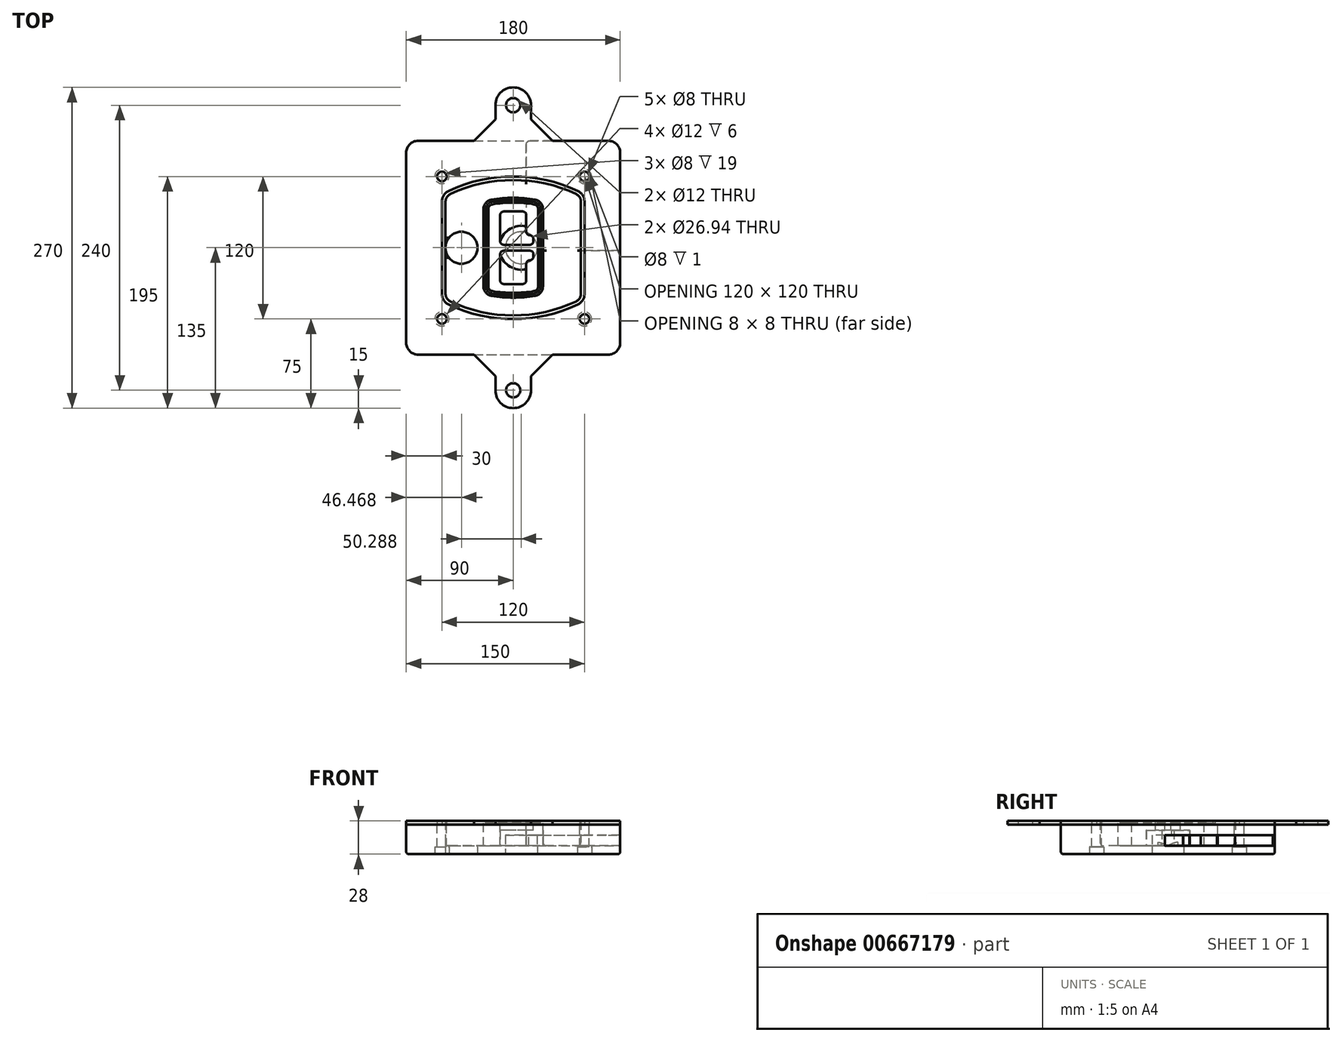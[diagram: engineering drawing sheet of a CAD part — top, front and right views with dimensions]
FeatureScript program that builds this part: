
annotation { "Feature Type Name" : "Feature", "Feature Type Description" : "" }
export const myFeature = defineFeature(function(context is Context, id is Id, definition is map)
    precondition{}
    {
        {
            var Q0;
            Q0=qCreatedBy(makeId("Top.planeOp"),FACE);
            var sketch = newSketch(context, id + "F0", { "sketchPlane" : qUnion([Q0])});
            skPoint(sketch, "E0.rect.middle", {"position": v(0, 0) * mm});
            skLineSegment(sketch, "E1.bottom", {"start": v(-80, -90) * mm, "end": v(80, -90) * mm});
            skLineSegment(sketch, "E1.top", {"start": v(-80, 90) * mm, "end": v(80, 90) * mm});
            skLineSegment(sketch, "E1.left", {"start": v(-90, -80) * mm, "end": v(-90, 80) * mm});
            skLineSegment(sketch, "E1.right", {"start": v(90, -80) * mm, "end": v(90, 80) * mm});
            skLineSegment(sketch, "E2", {"start": v(-90, 90) * mm, "end": v(90, -90) * mm, "construction": true});
            skLineSegment(sketch, "E3", {"start": v(90, 90) * mm, "end": v(-90, -90) * mm, "construction": true});
            skCircle(sketch, "E4", {"center": v(-60, 60) * mm, "radius": 4 * mm});
            skCircle(sketch, "E5", {"center": v(60, 60) * mm, "radius": 4 * mm});
            skCircle(sketch, "E6", {"center": v(60, -60) * mm, "radius": 4 * mm});
            skCircle(sketch, "E7", {"center": v(-60, -60) * mm, "radius": 4 * mm});
            skLineSegment(sketch, "E8", {"start": v(-60, 60) * mm, "end": v(60, 60) * mm, "construction": true});
            skLineSegment(sketch, "E9", {"start": v(60, 60) * mm, "end": v(60, -60) * mm, "construction": true});
            skLineSegment(sketch, "E10", {"start": v(60, -60) * mm, "end": v(-60, -60) * mm, "construction": true});
            skLineSegment(sketch, "E11", {"start": v(-60, -60) * mm, "end": v(-60, 60) * mm, "construction": true});
            skLineSegment(sketch, "E12", {"start": v(-60, 38.83) * mm, "end": v(-60, -38.83) * mm});
            skLineSegment(sketch, "E13", {"start": v(60, 38.83) * mm, "end": v(60, -38.83) * mm});
            skArc(sketch, "E14", {"start": v(54.26, 47.88) * mm, "mid": v(0, 60) * mm, "end": v(-54.26, 47.88) * mm});
            skArc(sketch, "E15", {"start": v(-54.26, -47.88) * mm, "mid": v(0, -60) * mm, "end": v(54.26, -47.88) * mm});
            skLineSegment(sketch, "E16", {"start": v(-60, 0) * mm, "end": v(60, 0) * mm, "construction": true});
            skPoint(sketch, "E17.visualSharp", {"position": v(-60, -45) * mm});
            skArc(sketch, "E17.filletArc", {"start": v(-60, -38.83) * mm, "mid": v(-58.44, -44.2) * mm, "end": v(-54.26, -47.88) * mm});
            skPoint(sketch, "E18.visualSharp", {"position": v(-60, 45) * mm});
            skArc(sketch, "E18.filletArc", {"start": v(-54.26, 47.88) * mm, "mid": v(-58.44, 44.2) * mm, "end": v(-60, 38.83) * mm});
            skPoint(sketch, "E19.visualSharp", {"position": v(60, 45) * mm});
            skArc(sketch, "E19.filletArc", {"start": v(60, 38.83) * mm, "mid": v(58.44, 44.2) * mm, "end": v(54.26, 47.88) * mm});
            skPoint(sketch, "E20.visualSharp", {"position": v(60, -45) * mm});
            skArc(sketch, "E20.filletArc", {"start": v(54.26, -47.88) * mm, "mid": v(58.44, -44.2) * mm, "end": v(60, -38.83) * mm});
            skPoint(sketch, "E21.visualSharp", {"position": v(-90, 90) * mm});
            skArc(sketch, "E21.filletArc", {"start": v(-80, 90) * mm, "mid": v(-87.07, 87.07) * mm, "end": v(-90, 80) * mm});
            skPoint(sketch, "E22.visualSharp", {"position": v(90, 90) * mm});
            skArc(sketch, "E22.filletArc", {"start": v(90, 80) * mm, "mid": v(87.07, 87.07) * mm, "end": v(80, 90) * mm});
            skPoint(sketch, "E23.visualSharp", {"position": v(90, -90) * mm});
            skArc(sketch, "E23.filletArc", {"start": v(80, -90) * mm, "mid": v(87.07, -87.07) * mm, "end": v(90, -80) * mm});
            skPoint(sketch, "E24.visualSharp", {"position": v(-90, -90) * mm});
            skArc(sketch, "E24.filletArc", {"start": v(-90, -80) * mm, "mid": v(-87.07, -87.07) * mm, "end": v(-80, -90) * mm});
            skArc(sketch, "E25.0", {"start": v(57, 38.83) * mm, "mid": v(55.9, 42.58) * mm, "end": v(52.98, 45.17) * mm});
            skLineSegment(sketch, "E25.1", {"start": v(57, 38.83) * mm, "end": v(57, -38.83) * mm});
            skArc(sketch, "E25.2", {"start": v(52.98, -45.17) * mm, "mid": v(55.9, -42.58) * mm, "end": v(57, -38.83) * mm});
            skArc(sketch, "E25.3", {"start": v(-52.98, -45.17) * mm, "mid": v(0, -57) * mm, "end": v(52.98, -45.17) * mm});
            skArc(sketch, "E25.4", {"start": v(-57, -38.83) * mm, "mid": v(-55.9, -42.58) * mm, "end": v(-52.98, -45.17) * mm});
            skArc(sketch, "E25.5", {"start": v(52.98, 45.17) * mm, "mid": v(0, 57) * mm, "end": v(-52.98, 45.17) * mm});
            skLineSegment(sketch, "E25.6", {"start": v(-57, 38.83) * mm, "end": v(-57, -38.83) * mm});
            skArc(sketch, "E25.7", {"start": v(-52.98, 45.17) * mm, "mid": v(-55.9, 42.58) * mm, "end": v(-57, 38.83) * mm});
            skArc(sketch, "E26.0", {"start": v(-55.96, 51.5) * mm, "mid": v(-61.82, 46.33) * mm, "end": v(-64, 38.83) * mm});
            skArc(sketch, "E26.1", {"start": v(55.96, 51.5) * mm, "mid": v(0, 64) * mm, "end": v(-55.96, 51.5) * mm});
            skArc(sketch, "E26.2", {"start": v(64, 38.83) * mm, "mid": v(61.82, 46.33) * mm, "end": v(55.96, 51.5) * mm});
            skLineSegment(sketch, "E26.3", {"start": v(64, 38.83) * mm, "end": v(64, -38.83) * mm});
            skArc(sketch, "E26.4", {"start": v(55.96, -51.5) * mm, "mid": v(61.82, -46.33) * mm, "end": v(64, -38.83) * mm});
            skLineSegment(sketch, "E26.5", {"start": v(-64, 38.83) * mm, "end": v(-64, -38.83) * mm});
            skArc(sketch, "E26.6", {"start": v(-55.96, -51.5) * mm, "mid": v(0, -64) * mm, "end": v(55.96, -51.5) * mm});
            skArc(sketch, "E26.7", {"start": v(-64, -38.83) * mm, "mid": v(-61.82, -46.33) * mm, "end": v(-55.96, -51.5) * mm});
            skSolve(sketch);
        }
        {
            var Q0;
            Q0=makeQuery(id+"F0.imprint","IMPRINT",FACE,{"disambiguationData":[TD([[makeQuery(id+"F0.imprint","IMPRINT",EDGE,{"derivedFrom":sQuery(id+"F0.wireOp",EDGE,"E1.bottom")}),1.0]])]});
            var Q1;
            Q1=makeQuery(id+"F0.imprint","IMPRINT",FACE,{"disambiguationData":[TD([[makeQuery(id+"F0.imprint","IMPRINT",EDGE,{"derivedFrom":sQuery(id+"F0.wireOp",EDGE,"E12")}),1.0]])]});
            var Q2;
            Q2=makeQuery(id+"F0.imprint","IMPRINT",FACE,{"disambiguationData":[TD([[makeQuery(id+"F0.imprint","IMPRINT",EDGE,{"derivedFrom":sQuery(id+"F0.wireOp",EDGE,"E25.0")}),1.0]])]});
            var Q3;
            Q3=makeQuery(id+"F0.imprint","IMPRINT",FACE,{"disambiguationData":[TD([[makeQuery(id+"F0.imprint","IMPRINT",EDGE,{"derivedFrom":sQuery(id+"F0.wireOp",EDGE,"E12")}),-1.0]])]});
            extrude(context, id + "F1", {"entities" : qUnion([Q0, Q1, Q2, Q3]), "oppositeDirection" : true, "depth" : 25 * mm, "offsetDistance" : 25 * mm});
        }
        {
            var Q0;
            Q0=makeQuery(id+"F0.imprint","IMPRINT",FACE,{"disambiguationData":[TD([[makeQuery(id+"F0.imprint","IMPRINT",EDGE,{"derivedFrom":sQuery(id+"F0.wireOp",EDGE,"E12")}),1.0]])]});
            extrude(context, id + "F2", {"entities" : qUnion([Q0]), "operationType" : NewBodyOperationType.ADD, "depth" : 3 * mm});
        }
        {
            var Q0;
            Q0=makeQuery(id+"F0.imprint","IMPRINT",FACE,{"disambiguationData":[TD([[makeQuery(id+"F0.imprint","IMPRINT",EDGE,{"derivedFrom":sQuery(id+"F0.wireOp",EDGE,"E25.0")}),1.0]])]});
            extrude(context, id + "F3", {"entities" : qUnion([Q0]), "operationType" : NewBodyOperationType.REMOVE, "oppositeDirection" : true, "depth" : 18 * mm});
        }
        {
            var Q0;
            Q0=makeQuery(id+"F2.opExtrude","CAP_FACE",FACE,{"disambiguationData":[OSD([sQuery(id+"F0.wireOp",EDGE,"E12"),sQuery(id+"F0.wireOp",EDGE,"E13"),sQuery(id+"F0.wireOp",EDGE,"E14"),sQuery(id+"F0.wireOp",EDGE,"E15"),sQuery(id+"F0.wireOp",EDGE,"E17.filletArc"),sQuery(id+"F0.wireOp",EDGE,"E18.filletArc"),sQuery(id+"F0.wireOp",EDGE,"E19.filletArc"),sQuery(id+"F0.wireOp",EDGE,"E20.filletArc"),sQuery(id+"F0.wireOp",EDGE,"E25.0"),sQuery(id+"F0.wireOp",EDGE,"E25.1"),sQuery(id+"F0.wireOp",EDGE,"E25.2"),sQuery(id+"F0.wireOp",EDGE,"E25.3"),sQuery(id+"F0.wireOp",EDGE,"E25.4"),sQuery(id+"F0.wireOp",EDGE,"E25.5"),sQuery(id+"F0.wireOp",EDGE,"E25.6"),sQuery(id+"F0.wireOp",EDGE,"E25.7")])],"isStart":false});
            var sketch = newSketch(context, id + "F4", { "sketchPlane" : qUnion([Q0])});
            skArc(sketch, "E27.0", {"start": v(-18.34, -40.45) * mm, "mid": v(0, -42) * mm, "end": v(18.34, -40.45) * mm});
            skArc(sketch, "E28.0", {"start": v(18.34, 40.45) * mm, "mid": v(0, 42) * mm, "end": v(-18.34, 40.45) * mm});
            skLineSegment(sketch, "E29", {"start": v(-25, 32.57) * mm, "end": v(-25, -32.57) * mm});
            skLineSegment(sketch, "E30", {"start": v(25, 32.57) * mm, "end": v(25, -32.57) * mm});
            skLineSegment(sketch, "E31", {"start": v(-25, 39.1) * mm, "end": v(25, 39.1) * mm, "construction": true});
            skLineSegment(sketch, "E32", {"start": v(-25, -39.1) * mm, "end": v(25, -39.1) * mm, "construction": true});
            skPoint(sketch, "E33.visualSharp", {"position": v(-25, 39.1) * mm});
            skArc(sketch, "E33.filletArc", {"start": v(-18.34, 40.45) * mm, "mid": v(-23.11, 37.73) * mm, "end": v(-25, 32.57) * mm});
            skPoint(sketch, "E34.visualSharp", {"position": v(25, 39.1) * mm});
            skArc(sketch, "E34.filletArc", {"start": v(25, 32.57) * mm, "mid": v(23.11, 37.73) * mm, "end": v(18.34, 40.45) * mm});
            skPoint(sketch, "E35.visualSharp", {"position": v(25, -39.1) * mm});
            skArc(sketch, "E35.filletArc", {"start": v(18.34, -40.45) * mm, "mid": v(23.11, -37.73) * mm, "end": v(25, -32.57) * mm});
            skPoint(sketch, "E36.visualSharp", {"position": v(-25, -39.1) * mm});
            skArc(sketch, "E36.filletArc", {"start": v(-25, -32.57) * mm, "mid": v(-23.11, -37.73) * mm, "end": v(-18.34, -40.45) * mm});
            skArc(sketch, "E37.0", {"start": v(52.98, 45.17) * mm, "mid": v(0, 57) * mm, "end": v(-52.98, 45.17) * mm});
            skArc(sketch, "E37.1", {"start": v(-52.98, 45.17) * mm, "mid": v(-55.9, 42.58) * mm, "end": v(-57, 38.83) * mm});
            skLineSegment(sketch, "E37.2", {"start": v(-57, 38.83) * mm, "end": v(-57, -38.83) * mm});
            skArc(sketch, "E37.3", {"start": v(-57, -38.83) * mm, "mid": v(-55.9, -42.58) * mm, "end": v(-52.98, -45.17) * mm});
            skArc(sketch, "E37.4", {"start": v(-52.98, -45.17) * mm, "mid": v(0, -57) * mm, "end": v(52.98, -45.17) * mm});
            skArc(sketch, "E37.5", {"start": v(52.98, -45.17) * mm, "mid": v(55.9, -42.58) * mm, "end": v(57, -38.83) * mm});
            skLineSegment(sketch, "E37.6", {"start": v(57, 38.83) * mm, "end": v(57, -38.83) * mm});
            skArc(sketch, "E37.7", {"start": v(57, 38.83) * mm, "mid": v(55.9, 42.58) * mm, "end": v(52.98, 45.17) * mm});
            skLineSegment(sketch, "E38.0", {"start": v(23, 32.57) * mm, "end": v(23, -32.57) * mm});
            skArc(sketch, "E38.1", {"start": v(18, -38.48) * mm, "mid": v(21.58, -36.44) * mm, "end": v(23, -32.57) * mm});
            skArc(sketch, "E38.2", {"start": v(-18, -38.48) * mm, "mid": v(0, -40) * mm, "end": v(18, -38.48) * mm});
            skArc(sketch, "E38.3", {"start": v(-23, -32.57) * mm, "mid": v(-21.58, -36.44) * mm, "end": v(-18, -38.48) * mm});
            skLineSegment(sketch, "E38.4", {"start": v(-23, 32.57) * mm, "end": v(-23, -32.57) * mm});
            skArc(sketch, "E38.5", {"start": v(23, 32.57) * mm, "mid": v(21.58, 36.44) * mm, "end": v(18, 38.48) * mm});
            skArc(sketch, "E38.6", {"start": v(-18, 38.48) * mm, "mid": v(-21.58, 36.44) * mm, "end": v(-23, 32.57) * mm});
            skArc(sketch, "E38.7", {"start": v(18, 38.48) * mm, "mid": v(0, 40) * mm, "end": v(-18, 38.48) * mm});
            skArc(sketch, "E39.0", {"start": v(21, 32.57) * mm, "mid": v(20.06, 35.15) * mm, "end": v(17.67, 36.5) * mm});
            skLineSegment(sketch, "E39.1", {"start": v(21, 32.57) * mm, "end": v(21, -32.57) * mm});
            skArc(sketch, "E39.2", {"start": v(17.67, -36.5) * mm, "mid": v(20.06, -35.15) * mm, "end": v(21, -32.57) * mm});
            skArc(sketch, "E39.3", {"start": v(-17.67, -36.5) * mm, "mid": v(0, -38) * mm, "end": v(17.67, -36.5) * mm});
            skArc(sketch, "E39.4", {"start": v(-21, -32.57) * mm, "mid": v(-20.06, -35.15) * mm, "end": v(-17.67, -36.5) * mm});
            skArc(sketch, "E39.5", {"start": v(17.67, 36.5) * mm, "mid": v(0, 38) * mm, "end": v(-17.67, 36.5) * mm});
            skLineSegment(sketch, "E39.6", {"start": v(-21, 32.57) * mm, "end": v(-21, -32.57) * mm});
            skArc(sketch, "E39.7", {"start": v(-17.67, 36.5) * mm, "mid": v(-20.06, 35.15) * mm, "end": v(-21, 32.57) * mm});
            skLineSegment(sketch, "E40", {"start": v(-25, 0) * mm, "end": v(25, 0) * mm, "construction": true});
            skLineSegment(sketch, "E41", {"start": v(-11, 5.5) * mm, "end": v(-11, 27.5) * mm});
            skLineSegment(sketch, "E42", {"start": v(-8, 30.5) * mm, "end": v(8, 30.5) * mm});
            skLineSegment(sketch, "E43", {"start": v(11, 27.5) * mm, "end": v(11, 13.5) * mm});
            skLineSegment(sketch, "E44", {"start": v(14, 10.5) * mm, "end": v(14, 10.5) * mm});
            skLineSegment(sketch, "E45", {"start": v(17, 7.5) * mm, "end": v(17, 5.5) * mm});
            skLineSegment(sketch, "E46", {"start": v(14, 2.5) * mm, "end": v(-8, 2.5) * mm});
            skPoint(sketch, "E47.visualSharp", {"position": v(-11, 30.5) * mm});
            skArc(sketch, "E47.filletArc", {"start": v(-8, 30.5) * mm, "mid": v(-10.12, 29.62) * mm, "end": v(-11, 27.5) * mm});
            skPoint(sketch, "E48.visualSharp", {"position": v(11, 30.5) * mm});
            skArc(sketch, "E48.filletArc", {"start": v(11, 27.5) * mm, "mid": v(10.12, 29.62) * mm, "end": v(8, 30.5) * mm});
            skPoint(sketch, "E49.visualSharp", {"position": v(11, 10.5) * mm});
            skArc(sketch, "E49.filletArc", {"start": v(11, 13.5) * mm, "mid": v(11.88, 11.38) * mm, "end": v(14, 10.5) * mm});
            skPoint(sketch, "E50.visualSharp", {"position": v(17, 10.5) * mm});
            skArc(sketch, "E50.filletArc", {"start": v(17, 7.5) * mm, "mid": v(16.12, 9.62) * mm, "end": v(14, 10.5) * mm});
            skPoint(sketch, "E51.visualSharp", {"position": v(17, 2.5) * mm});
            skArc(sketch, "E51.filletArc", {"start": v(14, 2.5) * mm, "mid": v(16.12, 3.38) * mm, "end": v(17, 5.5) * mm});
            skPoint(sketch, "E52.visualSharp", {"position": v(-11, 2.5) * mm});
            skArc(sketch, "E52.filletArc", {"start": v(-11, 5.5) * mm, "mid": v(-10.12, 3.38) * mm, "end": v(-8, 2.5) * mm});
            skLineSegment(sketch, "E53.0.MirrorCS", {"start": v(14, -2.5) * mm, "end": v(-8, -2.5) * mm});
            skArc(sketch, "E54.0.MirrorCS", {"start": v(-11, -5.5) * mm, "mid": v(-10.12, -3.38) * mm, "end": v(-8, -2.5) * mm});
            skLineSegment(sketch, "E55.0.MirrorCS", {"start": v(-11, -5.5) * mm, "end": v(-11, -27.5) * mm});
            skArc(sketch, "E56.0.MirrorCS", {"start": v(-8, -30.5) * mm, "mid": v(-10.12, -29.62) * mm, "end": v(-11, -27.5) * mm});
            skLineSegment(sketch, "E57.0.MirrorCS", {"start": v(-8, -30.5) * mm, "end": v(8, -30.5) * mm});
            skArc(sketch, "E58.0.MirrorCS", {"start": v(11, -27.5) * mm, "mid": v(10.12, -29.62) * mm, "end": v(8, -30.5) * mm});
            skLineSegment(sketch, "E59.0.MirrorCS", {"start": v(11, -27.5) * mm, "end": v(11, -13.5) * mm});
            skArc(sketch, "E60.0.MirrorCS", {"start": v(11, -13.5) * mm, "mid": v(11.88, -11.38) * mm, "end": v(14, -10.5) * mm});
            skArc(sketch, "E61.0.MirrorCS", {"start": v(17, -7.5) * mm, "mid": v(16.12, -9.62) * mm, "end": v(14, -10.5) * mm});
            skLineSegment(sketch, "E62.0.MirrorCS", {"start": v(17, -7.5) * mm, "end": v(17, -5.5) * mm});
            skArc(sketch, "E63.0.MirrorCS", {"start": v(14, -2.5) * mm, "mid": v(16.12, -3.38) * mm, "end": v(17, -5.5) * mm});
            skSolve(sketch);
        }
        {
            var Q0;
            Q0=makeQuery(id+"F4.imprint","IMPRINT",FACE,{"disambiguationData":[TD([[makeQuery(id+"F4.imprint","IMPRINT",EDGE,{"derivedFrom":sQuery(id+"F4.wireOp",EDGE,"E27.0")}),1.0]])]});
            var Q1;
            Q1=makeQuery(id+"F4.imprint","IMPRINT",FACE,{"disambiguationData":[TD([[makeQuery(id+"F4.imprint","IMPRINT",EDGE,{"derivedFrom":sQuery(id+"F4.wireOp",EDGE,"E38.0")}),-1.0]])]});
            var Q2;
            Q2=makeQuery(id+"F4.imprint","IMPRINT",FACE,{"disambiguationData":[TD([[makeQuery(id+"F4.imprint","IMPRINT",EDGE,{"derivedFrom":sQuery(id+"F4.wireOp",EDGE,"E39.0")}),1.0]])]});
            extrude(context, id + "F5", {"entities" : qUnion([Q0, Q1, Q2]), "operationType" : NewBodyOperationType.ADD, "endBound" : BoundingType.UP_TO_NEXT, "oppositeDirection" : true, "depth" : 25 * mm});
        }
        {
            var Q0;
            Q0=makeQuery(id+"F4.imprint","IMPRINT",FACE,{"disambiguationData":[TD([[makeQuery(id+"F4.imprint","IMPRINT",EDGE,{"derivedFrom":sQuery(id+"F4.wireOp",EDGE,"E38.0")}),-1.0]])]});
            extrude(context, id + "F6", {"entities" : qUnion([Q0]), "operationType" : NewBodyOperationType.REMOVE, "oppositeDirection" : true, "depth" : 2 * mm});
        }
        {
            var Q0;
            Q0=makeQuery(id+"F1.opExtrude","CAP_FACE",FACE,{"disambiguationData":[OSD([sQuery(id+"F0.wireOp",EDGE,"E1.bottom"),sQuery(id+"F0.wireOp",EDGE,"E1.top"),sQuery(id+"F0.wireOp",EDGE,"E1.left"),sQuery(id+"F0.wireOp",EDGE,"E1.right"),sQuery(id+"F0.wireOp",EDGE,"E4"),sQuery(id+"F0.wireOp",EDGE,"E5"),sQuery(id+"F0.wireOp",EDGE,"E6"),sQuery(id+"F0.wireOp",EDGE,"E7"),sQuery(id+"F0.wireOp",EDGE,"E21.filletArc"),sQuery(id+"F0.wireOp",EDGE,"E22.filletArc"),sQuery(id+"F0.wireOp",EDGE,"E23.filletArc"),sQuery(id+"F0.wireOp",EDGE,"E24.filletArc")])],"isStart":false});
            var sketch = newSketch(context, id + "F7", { "sketchPlane" : qUnion([Q0])});
            skCircle(sketch, "E64", {"center": v(6.76, 0) * mm, "radius": 13.47 * mm});
            skCircle(sketch, "E65", {"center": v(-43.53, 0) * mm, "radius": 13.47 * mm});
            skLineSegment(sketch, "E66", {"start": v(90, 0) * mm, "end": v(-90, 0) * mm});
            skCircle(sketch, "E67", {"center": v(6.76, 0) * mm, "radius": 18.47 * mm});
            skCircle(sketch, "E68", {"center": v(60, -60) * mm, "radius": 6 * mm});
            skCircle(sketch, "E69", {"center": v(-60, -60) * mm, "radius": 6 * mm});
            skCircle(sketch, "E70", {"center": v(-60, 60) * mm, "radius": 6 * mm});
            skCircle(sketch, "E71", {"center": v(60, 60) * mm, "radius": 6 * mm});
            skSolve(sketch);
        }
        {
            var Q0;
            {var subQ1=sQuery(id+"F7.wireOp",EDGE,"E66");var subQ4=sQuery(id+"F7.wireOp",EDGE,"E64");var subQ6=makeQuery(id+"F7.imprint","INTERSECT",VERTEX,{"disambiguationData":[OD(0.0)],"derivedFrom":[subQ4,subQ1]});Q0=makeQuery(id+"F7.imprint","IMPRINT",FACE,{"disambiguationData":[TD([[makeQuery(id+"F7.imprint","IMPRINT",EDGE,{"disambiguationData":[TD([[subQ6,-1.0]])],"derivedFrom":subQ4}),-1.0]])]});}
            var Q1;
            {var subQ0=sQuery(id+"F7.wireOp",EDGE,"E66");var subQ1=sQuery(id+"F7.wireOp",EDGE,"E64");var subQ3=makeQuery(id+"F7.imprint","INTERSECT",VERTEX,{"disambiguationData":[OD(0.0)],"derivedFrom":[subQ1,subQ0]});Q1=makeQuery(id+"F7.imprint","IMPRINT",FACE,{"disambiguationData":[TD([[makeQuery(id+"F7.imprint","IMPRINT",EDGE,{"disambiguationData":[TD([[subQ3,-1.0]])],"derivedFrom":subQ1}),1.0]])]});}
            var Q2;
            {var subQ0=sQuery(id+"F7.wireOp",EDGE,"E66");var subQ1=sQuery(id+"F7.wireOp",EDGE,"E64");var subQ3=makeQuery(id+"F7.imprint","INTERSECT",VERTEX,{"disambiguationData":[OD(0.0)],"derivedFrom":[subQ1,subQ0]});Q2=makeQuery(id+"F7.imprint","IMPRINT",FACE,{"disambiguationData":[TD([[makeQuery(id+"F7.imprint","IMPRINT",EDGE,{"disambiguationData":[TD([[subQ3,1.0]])],"derivedFrom":subQ1}),1.0]])]});}
            var Q3;
            {var subQ1=sQuery(id+"F7.wireOp",EDGE,"E66");var subQ4=sQuery(id+"F7.wireOp",EDGE,"E64");var subQ6=makeQuery(id+"F7.imprint","INTERSECT",VERTEX,{"disambiguationData":[OD(0.0)],"derivedFrom":[subQ4,subQ1]});Q3=makeQuery(id+"F7.imprint","IMPRINT",FACE,{"disambiguationData":[TD([[makeQuery(id+"F7.imprint","IMPRINT",EDGE,{"disambiguationData":[TD([[subQ6,1.0]])],"derivedFrom":subQ4}),-1.0]])]});}
            extrude(context, id + "F8", {"entities" : qUnion([Q0, Q1, Q2, Q3]), "operationType" : NewBodyOperationType.ADD, "oppositeDirection" : true, "depth" : 20 * mm});
        }
        {
            var Q0;
            {var subQ0=sQuery(id+"F7.wireOp",EDGE,"E66");var subQ1=sQuery(id+"F7.wireOp",EDGE,"E64");var subQ3=makeQuery(id+"F7.imprint","INTERSECT",VERTEX,{"disambiguationData":[OD(0.0)],"derivedFrom":[subQ1,subQ0]});Q0=makeQuery(id+"F7.imprint","IMPRINT",FACE,{"disambiguationData":[TD([[makeQuery(id+"F7.imprint","IMPRINT",EDGE,{"disambiguationData":[TD([[subQ3,-1.0]])],"derivedFrom":subQ1}),1.0]])]});}
            var Q1;
            {var subQ0=sQuery(id+"F7.wireOp",EDGE,"E66");var subQ1=sQuery(id+"F7.wireOp",EDGE,"E64");var subQ3=makeQuery(id+"F7.imprint","INTERSECT",VERTEX,{"disambiguationData":[OD(0.0)],"derivedFrom":[subQ1,subQ0]});Q1=makeQuery(id+"F7.imprint","IMPRINT",FACE,{"disambiguationData":[TD([[makeQuery(id+"F7.imprint","IMPRINT",EDGE,{"disambiguationData":[TD([[subQ3,1.0]])],"derivedFrom":subQ1}),1.0]])]});}
            extrude(context, id + "F9", {"entities" : qUnion([Q0, Q1]), "operationType" : NewBodyOperationType.REMOVE, "oppositeDirection" : true, "depth" : 16 * mm});
        }
        {
            var Q0;
            {var subQ0=sQuery(id+"F7.wireOp",EDGE,"E66");var subQ1=sQuery(id+"F7.wireOp",EDGE,"E65");var subQ3=makeQuery(id+"F7.imprint","INTERSECT",VERTEX,{"disambiguationData":[OD(0.0)],"derivedFrom":[subQ1,subQ0]});Q0=makeQuery(id+"F7.imprint","IMPRINT",FACE,{"disambiguationData":[TD([[makeQuery(id+"F7.imprint","IMPRINT",EDGE,{"disambiguationData":[TD([[subQ3,-1.0]])],"derivedFrom":subQ1}),1.0]])]});}
            var Q1;
            {var subQ0=sQuery(id+"F7.wireOp",EDGE,"E66");var subQ1=sQuery(id+"F7.wireOp",EDGE,"E65");var subQ3=makeQuery(id+"F7.imprint","INTERSECT",VERTEX,{"disambiguationData":[OD(0.0)],"derivedFrom":[subQ1,subQ0]});Q1=makeQuery(id+"F7.imprint","IMPRINT",FACE,{"disambiguationData":[TD([[makeQuery(id+"F7.imprint","IMPRINT",EDGE,{"disambiguationData":[TD([[subQ3,1.0]])],"derivedFrom":subQ1}),1.0]])]});}
            extrude(context, id + "F10", {"entities" : qUnion([Q0, Q1]), "operationType" : NewBodyOperationType.REMOVE, "oppositeDirection" : true, "depth" : 25 * mm});
        }
        {
            var Q0;
            Q0=makeQuery(id+"F7.imprint","IMPRINT",FACE,{"disambiguationData":[TD([[makeQuery(id+"F7.imprint","IMPRINT",EDGE,{"derivedFrom":sQuery(id+"F7.wireOp",EDGE,"E68")}),1.0]])]});
            var Q1;
            Q1=makeQuery(id+"F7.imprint","IMPRINT",FACE,{"disambiguationData":[TD([[makeQuery(id+"F7.imprint","IMPRINT",EDGE,{"derivedFrom":makeQuery(id+"F1.opExtrude","CAP_EDGE",EDGE,{"disambiguationData":[OSD([sQuery(id+"F0.wireOp",EDGE,"E5")])],"isStart":false})}),-1.0]])]});
            var Q2;
            Q2=makeQuery(id+"F7.imprint","IMPRINT",FACE,{"disambiguationData":[TD([[makeQuery(id+"F7.imprint","IMPRINT",EDGE,{"derivedFrom":sQuery(id+"F7.wireOp",EDGE,"E69")}),1.0]])]});
            var Q3;
            Q3=makeQuery(id+"F7.imprint","IMPRINT",FACE,{"disambiguationData":[TD([[makeQuery(id+"F7.imprint","IMPRINT",EDGE,{"derivedFrom":makeQuery(id+"F1.opExtrude","CAP_EDGE",EDGE,{"disambiguationData":[OSD([sQuery(id+"F0.wireOp",EDGE,"E4")])],"isStart":false})}),-1.0]])]});
            var Q4;
            Q4=makeQuery(id+"F7.imprint","IMPRINT",FACE,{"disambiguationData":[TD([[makeQuery(id+"F7.imprint","IMPRINT",EDGE,{"derivedFrom":sQuery(id+"F7.wireOp",EDGE,"E70")}),1.0]])]});
            var Q5;
            Q5=makeQuery(id+"F7.imprint","IMPRINT",FACE,{"disambiguationData":[TD([[makeQuery(id+"F7.imprint","IMPRINT",EDGE,{"derivedFrom":makeQuery(id+"F1.opExtrude","CAP_EDGE",EDGE,{"disambiguationData":[OSD([sQuery(id+"F0.wireOp",EDGE,"E7")])],"isStart":false})}),-1.0]])]});
            var Q6;
            Q6=makeQuery(id+"F7.imprint","IMPRINT",FACE,{"disambiguationData":[TD([[makeQuery(id+"F7.imprint","IMPRINT",EDGE,{"derivedFrom":sQuery(id+"F7.wireOp",EDGE,"E71")}),1.0]])]});
            var Q7;
            Q7=makeQuery(id+"F7.imprint","IMPRINT",FACE,{"disambiguationData":[TD([[makeQuery(id+"F7.imprint","IMPRINT",EDGE,{"derivedFrom":makeQuery(id+"F1.opExtrude","CAP_EDGE",EDGE,{"disambiguationData":[OSD([sQuery(id+"F0.wireOp",EDGE,"E6")])],"isStart":false})}),-1.0]])]});
            extrude(context, id + "F11", {"entities" : qUnion([Q0, Q1, Q2, Q3, Q4, Q5, Q6, Q7]), "operationType" : NewBodyOperationType.REMOVE, "oppositeDirection" : true, "depth" : 6 * mm});
        }
        {
            var Q0;
            Q0=makeQuery(id+"F9.boolean.opBoolean","COPY",FACE,{"derivedFrom":makeQuery(id+"F9.opExtrude","CAP_FACE",FACE,{"disambiguationData":[OSD([sQuery(id+"F7.wireOp",EDGE,"E64")])],"isStart":false})});
            var sketch = newSketch(context, id + "F12", { "sketchPlane" : qUnion([Q0])});
            skArc(sketch, "E72.0", {"start": v(11, -88.19) * mm, "mid": v(97.1, -83.6) * mm, "end": v(92.5, 2.5) * mm});
            skLineSegment(sketch, "E72.1", {"start": v(11, -17.97) * mm, "end": v(11, -17.97) * mm});
            skLineSegment(sketch, "E73", {"start": v(92.5, -105.13) * mm, "end": v(102.3, -105.13) * mm});
            skLineSegment(sketch, "E74.0", {"start": v(92.5, 2.5) * mm, "end": v(14, 2.5) * mm});
            skArc(sketch, "E74.1", {"start": v(14, 2.5) * mm, "mid": v(16.12, 3.38) * mm, "end": v(17, 5.5) * mm});
            skLineSegment(sketch, "E74.2", {"start": v(17, 7.5) * mm, "end": v(17, 5.5) * mm});
            skArc(sketch, "E74.3", {"start": v(17, 7.5) * mm, "mid": v(16.12, 9.62) * mm, "end": v(14, 10.5) * mm});
            skArc(sketch, "E74.4", {"start": v(11, 13.5) * mm, "mid": v(11.88, 11.38) * mm, "end": v(14, 10.5) * mm});
            skLineSegment(sketch, "E74.5", {"start": v(11, 13.5) * mm, "end": v(11, -88.19) * mm});
            skLineSegment(sketch, "E74.7", {"start": v(92.5, -2.5) * mm, "end": v(14, -2.5) * mm});
            skArc(sketch, "E74.8", {"start": v(14, -2.5) * mm, "mid": v(16.12, -3.38) * mm, "end": v(17, -5.5) * mm});
            skLineSegment(sketch, "E74.9", {"start": v(17, -7.5) * mm, "end": v(17, -5.5) * mm});
            skArc(sketch, "E74.10", {"start": v(17, -7.5) * mm, "mid": v(16.12, -9.62) * mm, "end": v(14, -10.5) * mm});
            skArc(sketch, "E74.11", {"start": v(11, -13.5) * mm, "mid": v(11.88, -11.38) * mm, "end": v(14, -10.5) * mm});
            skLineSegment(sketch, "E74.12", {"start": v(11, -17.97) * mm, "end": v(11, -13.5) * mm});
            skPoint(sketch, "E75.orphan", {"position": v(11, -27.5) * mm});
            skPoint(sketch, "E76.orphan", {"position": v(-8, -2.5) * mm});
            skPoint(sketch, "E77.orphan", {"position": v(-8, 2.5) * mm});
            skPoint(sketch, "E78.orphan", {"position": v(11, 27.5) * mm});
            skSolve(sketch);
        }
        {
            var Q0;
            {var subQ7=sQuery(id+"F12.wireOp",EDGE,"E72.0");var subQ14=sQuery(id+"F12.wireOp",EDGE,"E72.1");var subQ16=sQuery(id+"F12.wireOp",EDGE,"E74.1");var subQ18=sQuery(id+"F12.wireOp",EDGE,"E74.8");Q0=qUnion([makeQuery(id+"F12.imprint","IMPRINT",FACE,{"disambiguationData":[TD([[makeQuery(id+"F12.imprint","IMPRINT",EDGE,{"derivedFrom":subQ7}),1.0]])]}),makeQuery(id+"F12.imprint","IMPRINT",FACE,{"disambiguationData":[TD([[makeQuery(id+"F12.imprint","IMPRINT",EDGE,{"derivedFrom":subQ14}),1.0]])]}),makeQuery(id+"F12.imprint","IMPRINT",FACE,{"disambiguationData":[TD([[makeQuery(id+"F12.imprint","IMPRINT",EDGE,{"derivedFrom":subQ16}),1.0]])]}),makeQuery(id+"F12.imprint","IMPRINT",FACE,{"disambiguationData":[TD([[makeQuery(id+"F12.imprint","IMPRINT",EDGE,{"derivedFrom":subQ18}),-1.0]])]})]);}
            var Q1;
            Q1=makeQuery(id+"F5.boolean.opBoolean","SPLIT",FACE,{"disambiguationData":[TD([makeQuery(id+"F5.opExtrude","SWEPT_FACE",FACE,{"disambiguationData":[OSD([sQuery(id+"F4.wireOp",EDGE,"E41")])]})])],"derivedFrom":makeQuery(id+"F3.boolean.opBoolean","COPY",FACE,{"derivedFrom":makeQuery(id+"F3.opExtrude","CAP_FACE",FACE,{"disambiguationData":[OSD([sQuery(id+"F0.wireOp",EDGE,"E25.0"),sQuery(id+"F0.wireOp",EDGE,"E25.1"),sQuery(id+"F0.wireOp",EDGE,"E25.2"),sQuery(id+"F0.wireOp",EDGE,"E25.3"),sQuery(id+"F0.wireOp",EDGE,"E25.4"),sQuery(id+"F0.wireOp",EDGE,"E25.5"),sQuery(id+"F0.wireOp",EDGE,"E25.6"),sQuery(id+"F0.wireOp",EDGE,"E25.7")])],"isStart":false})})});
            extrude(context, id + "F13", {"entities" : qUnion([Q0]), "operationType" : NewBodyOperationType.REMOVE, "endBound" : BoundingType.UP_TO_SURFACE, "endBoundEntityFace" : qUnion([Q1]), "depth" : 25 * mm});
        }
        {
            var Q0;
            Q0=makeQuery(id+"F3.boolean.opBoolean","COPY",EDGE,{"derivedFrom":makeQuery(id+"F3.opExtrude","CAP_EDGE",EDGE,{"disambiguationData":[OSD([sQuery(id+"F0.wireOp",EDGE,"E25.6")])],"isStart":false})});
            var Q1;
            Q1=makeQuery(id+"F8.boolean.opBoolean","INTERSECT",EDGE,{"derivedFrom":[makeQuery(id+"F5.opExtrude","SWEPT_FACE",FACE,{"disambiguationData":[OSD([sQuery(id+"F4.wireOp",EDGE,"E30")])]}),makeQuery(id+"F8.opExtrude","CAP_FACE",FACE,{"disambiguationData":[OSD([sQuery(id+"F7.wireOp",EDGE,"E67")])],"isStart":false})]});
            var Q2;
            Q2=makeQuery(id+"F8.boolean.opBoolean","INTERSECT",EDGE,{"disambiguationData":[OD(1.0)],"derivedFrom":[makeQuery(id+"F5.opExtrude","SWEPT_FACE",FACE,{"disambiguationData":[OSD([sQuery(id+"F4.wireOp",EDGE,"E30")])]}),makeQuery(id+"F8.opExtrude","SWEPT_FACE",FACE,{"disambiguationData":[OSD([sQuery(id+"F7.wireOp",EDGE,"E67")])]})]});
            var Q3;
            {var subQ0=makeQuery(id+"F3.boolean.opBoolean","COPY",FACE,{"derivedFrom":makeQuery(id+"F3.opExtrude","CAP_FACE",FACE,{"disambiguationData":[OSD([sQuery(id+"F0.wireOp",EDGE,"E25.0"),sQuery(id+"F0.wireOp",EDGE,"E25.1"),sQuery(id+"F0.wireOp",EDGE,"E25.2"),sQuery(id+"F0.wireOp",EDGE,"E25.3"),sQuery(id+"F0.wireOp",EDGE,"E25.4"),sQuery(id+"F0.wireOp",EDGE,"E25.5"),sQuery(id+"F0.wireOp",EDGE,"E25.6"),sQuery(id+"F0.wireOp",EDGE,"E25.7")])],"isStart":false})});var subQ1=sQuery(id+"F4.wireOp",EDGE,"E30");Q3=makeQuery(id+"F8.boolean.opBoolean","SPLIT",EDGE,{"disambiguationData":[TD([makeQuery(id+"F5.opExtrude","SWEPT_FACE",FACE,{"disambiguationData":[OSD([sQuery(id+"F4.wireOp",EDGE,"E35.filletArc")])]})])],"derivedFrom":makeQuery(id+"F5.opExtrude","TWEAK_EDGE",EDGE,{"derivedFrom":[subQ0,makeQuery(id+"F4.imprint","IMPRINT",EDGE,{"derivedFrom":subQ1})]})});}
            var Q4;
            {var subQ0=sQuery(id+"F0.wireOp",EDGE,"E25.0");var subQ1=sQuery(id+"F0.wireOp",EDGE,"E25.1");var subQ2=sQuery(id+"F0.wireOp",EDGE,"E25.2");var subQ3=sQuery(id+"F0.wireOp",EDGE,"E25.3");var subQ4=sQuery(id+"F0.wireOp",EDGE,"E25.4");var subQ5=sQuery(id+"F0.wireOp",EDGE,"E25.5");var subQ6=sQuery(id+"F0.wireOp",EDGE,"E25.6");var subQ7=sQuery(id+"F0.wireOp",EDGE,"E25.7");Q4=makeQuery(id+"F8.boolean.opBoolean","INTERSECT",EDGE,{"derivedFrom":[makeQuery(id+"F5.boolean.opBoolean","SPLIT",FACE,{"disambiguationData":[TD([makeQuery(id+"F2.opExtrude","SWEPT_FACE",FACE,{"disambiguationData":[OSD([subQ0])]})])],"derivedFrom":makeQuery(id+"F3.boolean.opBoolean","COPY",FACE,{"derivedFrom":makeQuery(id+"F3.opExtrude","CAP_FACE",FACE,{"disambiguationData":[OSD([subQ0,subQ1,subQ2,subQ3,subQ4,subQ5,subQ6,subQ7])],"isStart":false})})}),makeQuery(id+"F8.opExtrude","SWEPT_FACE",FACE,{"disambiguationData":[OSD([sQuery(id+"F7.wireOp",EDGE,"E67")])]})]});}
            var Q5;
            Q5=makeQuery(id+"F8.boolean.opBoolean","INTERSECT",EDGE,{"disambiguationData":[OD(0.0)],"derivedFrom":[makeQuery(id+"F5.opExtrude","SWEPT_FACE",FACE,{"disambiguationData":[OSD([sQuery(id+"F4.wireOp",EDGE,"E30")])]}),makeQuery(id+"F8.opExtrude","SWEPT_FACE",FACE,{"disambiguationData":[OSD([sQuery(id+"F7.wireOp",EDGE,"E67")])]})]});
            fillet(context, id + "F14", {"entities" : qUnion([Q0, Q1, Q2, Q3, Q4, Q5]), "radius" : 3 * mm, "tangentPropagation" : true, "allowEdgeOverflow" : false});
        }
        {
            var Q0;
            Q0=makeQuery(id+"F1.opExtrude","CAP_EDGE",EDGE,{"disambiguationData":[OSD([sQuery(id+"F0.wireOp",EDGE,"E1.bottom")])],"isStart":false});
            fillet(context, id + "F15", {"entities" : qUnion([Q0]), "radius" : 2 * mm, "tangentPropagation" : true, "allowEdgeOverflow" : false});
        }
        {
            var Q0;
            {var subQ0=sQuery(id+"F0.wireOp",EDGE,"E21.filletArc");var subQ1=sQuery(id+"F0.wireOp",EDGE,"E7");var subQ2=sQuery(id+"F0.wireOp",EDGE,"E6");var subQ3=sQuery(id+"F0.wireOp",EDGE,"E5");var subQ4=sQuery(id+"F0.wireOp",EDGE,"E4");var subQ5=sQuery(id+"F0.wireOp",EDGE,"E22.filletArc");var subQ6=sQuery(id+"F0.wireOp",EDGE,"E1.bottom");var subQ7=sQuery(id+"F0.wireOp",EDGE,"E1.right");var subQ8=sQuery(id+"F0.wireOp",EDGE,"E1.top");var subQ9=sQuery(id+"F0.wireOp",EDGE,"E1.left");var subQ10=sQuery(id+"F0.wireOp",EDGE,"E23.filletArc");var subQ11=sQuery(id+"F0.wireOp",EDGE,"E24.filletArc");Q0=makeQuery(id+"F2.boolean.opBoolean","SPLIT",FACE,{"disambiguationData":[TD([makeQuery(id+"F1.opExtrude","SWEPT_FACE",FACE,{"disambiguationData":[OSD([subQ6])]})])],"derivedFrom":makeQuery(id+"F1.opExtrude","CAP_FACE",FACE,{"disambiguationData":[OSD([subQ6,subQ8,subQ9,subQ7,subQ4,subQ3,subQ2,subQ1,subQ0,subQ5,subQ10,subQ11])],"isStart":true})});}
            var sketch = newSketch(context, id + "F16", { "sketchPlane" : qUnion([Q0])});
            skCircle(sketch, "E79", {"center": v(0, 120) * mm, "radius": 6 * mm});
            skLineSegment(sketch, "E80", {"start": v(-33, 90) * mm, "end": v(-15, 108) * mm});
            skLineSegment(sketch, "E81", {"start": v(33, 90) * mm, "end": v(15, 108) * mm});
            skArc(sketch, "E82", {"start": v(15, 120) * mm, "mid": v(0, 135) * mm, "end": v(-15, 120) * mm});
            skLineSegment(sketch, "E83", {"start": v(-15, 120) * mm, "end": v(-15, 108) * mm});
            skLineSegment(sketch, "E84", {"start": v(15, 120) * mm, "end": v(15, 108) * mm});
            skLineSegment(sketch, "E85", {"start": v(0, -90) * mm, "end": v(0, -120) * mm});
            skCircle(sketch, "E86", {"center": v(0, -120) * mm, "radius": 6 * mm});
            skLineSegment(sketch, "E87", {"start": v(-15, -108) * mm, "end": v(-33, -90) * mm});
            skLineSegment(sketch, "E88", {"start": v(-15, -120) * mm, "end": v(-15, -108) * mm});
            skArc(sketch, "E89", {"start": v(-15, -120) * mm, "mid": v(0, -135) * mm, "end": v(15, -120) * mm});
            skLineSegment(sketch, "E90", {"start": v(33, -90) * mm, "end": v(15, -108) * mm});
            skLineSegment(sketch, "E91", {"start": v(15, -120) * mm, "end": v(15, -108) * mm});
            skSolve(sketch);
        }
        {
            var Q0;
            Q0=makeQuery(id+"F16.imprint","IMPRINT",FACE,{"disambiguationData":[TD([[makeQuery(id+"F16.imprint","IMPRINT",EDGE,{"derivedFrom":sQuery(id+"F16.wireOp",EDGE,"E79")}),-1.0]])]});
            var Q1;
            Q1=makeQuery(id+"F16.imprint","IMPRINT",FACE,{"disambiguationData":[TD([[makeQuery(id+"F16.imprint","IMPRINT",EDGE,{"derivedFrom":sQuery(id+"F16.wireOp",EDGE,"E86")}),-1.0]])]});
            var Q2;
            Q2=makeQuery(id+"F16.imprint","IMPRINT",FACE,{"disambiguationData":[TD([[makeQuery(id+"F16.imprint","IMPRINT",EDGE,{"derivedFrom":makeQuery(id+"F1.opExtrude","CAP_EDGE",EDGE,{"disambiguationData":[OSD([sQuery(id+"F0.wireOp",EDGE,"E1.left")])],"isStart":true})}),-1.0]])]});
            var Q3;
            Q3=makeQuery(id+"F2.opExtrude","CAP_FACE",FACE,{"disambiguationData":[OSD([sQuery(id+"F0.wireOp",EDGE,"E12"),sQuery(id+"F0.wireOp",EDGE,"E13"),sQuery(id+"F0.wireOp",EDGE,"E14"),sQuery(id+"F0.wireOp",EDGE,"E15"),sQuery(id+"F0.wireOp",EDGE,"E17.filletArc"),sQuery(id+"F0.wireOp",EDGE,"E18.filletArc"),sQuery(id+"F0.wireOp",EDGE,"E19.filletArc"),sQuery(id+"F0.wireOp",EDGE,"E20.filletArc"),sQuery(id+"F0.wireOp",EDGE,"E25.0"),sQuery(id+"F0.wireOp",EDGE,"E25.1"),sQuery(id+"F0.wireOp",EDGE,"E25.2"),sQuery(id+"F0.wireOp",EDGE,"E25.3"),sQuery(id+"F0.wireOp",EDGE,"E25.4"),sQuery(id+"F0.wireOp",EDGE,"E25.5"),sQuery(id+"F0.wireOp",EDGE,"E25.6"),sQuery(id+"F0.wireOp",EDGE,"E25.7")])],"isStart":false});
            extrude(context, id + "F17", {"entities" : qUnion([Q0, Q1, Q2]), "endBound" : BoundingType.UP_TO_SURFACE, "depth" : 25 * mm, "endBoundEntityFace" : qUnion([Q3]), "offsetDistance" : 25 * mm});
        }
    });
